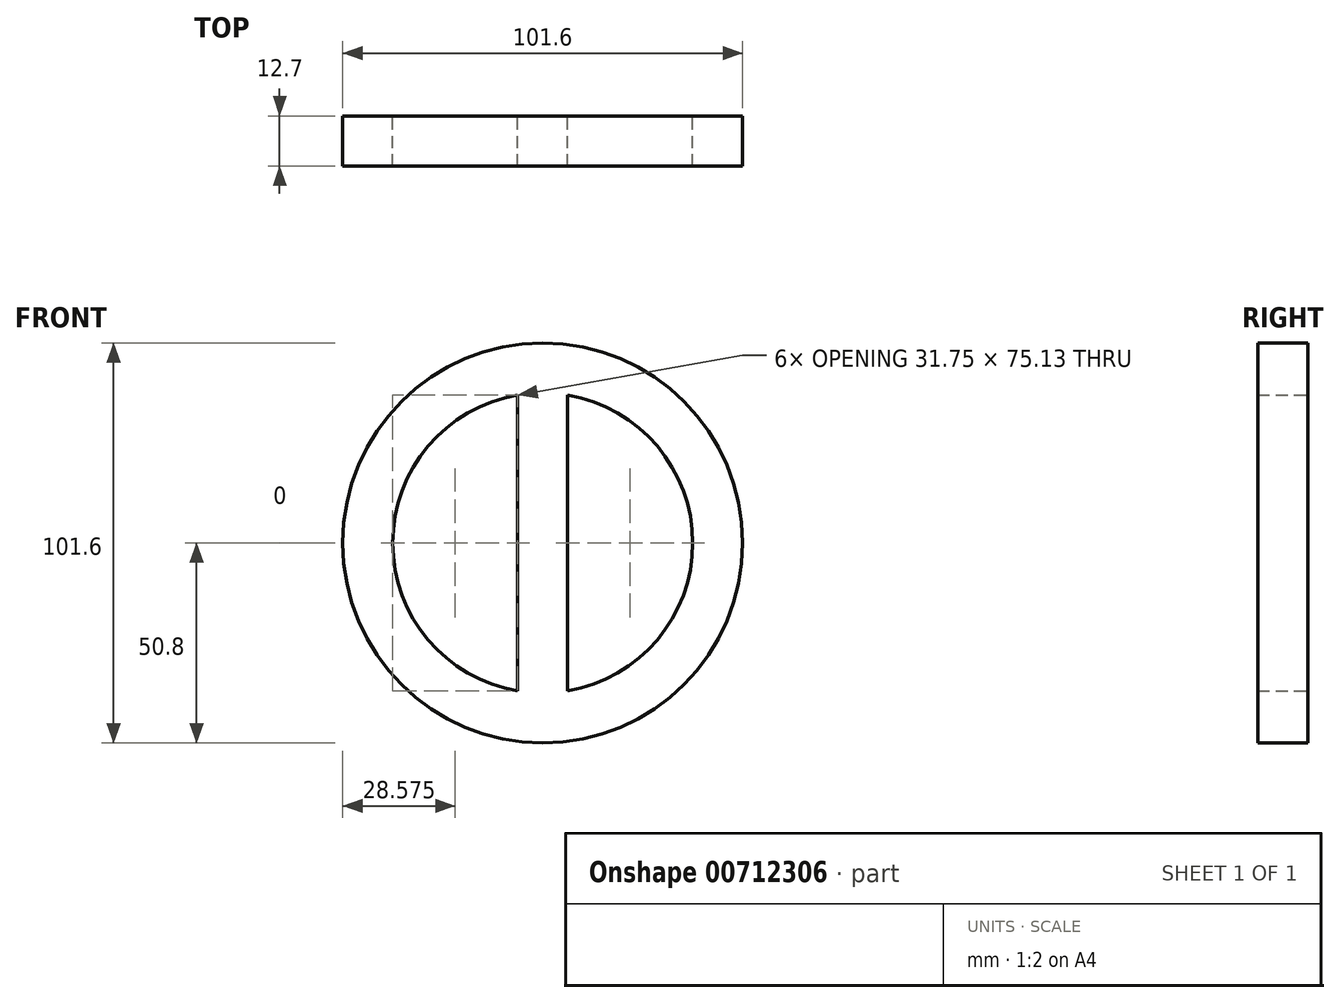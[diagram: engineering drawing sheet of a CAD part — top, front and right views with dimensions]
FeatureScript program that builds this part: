
annotation { "Feature Type Name" : "Feature", "Feature Type Description" : "" }
export const myFeature = defineFeature(function(context is Context, id is Id, definition is map)
    precondition{}
    {
        {
            var Q0;
            Q0=qCreatedBy(makeId("Front.planeOp"),FACE);
            var sketch = newSketch(context, id + "F0", { "sketchPlane" : qUnion([Q0])});
            skArc(sketch, "E0", {"start": v(-6.35, 37.57) * mm, "mid": v(-38.1, 0) * mm, "end": v(-6.35, -37.57) * mm});
            skCircle(sketch, "E1.0", {"center": v(0, 0) * mm, "radius": 50.8 * mm});
            skLineSegment(sketch, "E2.left", {"start": v(-6.35, 37.57) * mm, "end": v(-6.35, -37.57) * mm});
            skLineSegment(sketch, "E2.right", {"start": v(6.35, 37.57) * mm, "end": v(6.35, -37.57) * mm});
            skPoint(sketch, "E2.bottom.end.orphan", {"position": v(6.35, 40.14) * mm});
            skPoint(sketch, "E3.orphan", {"position": v(-6.35, 40.14) * mm});
            skArc(sketch, "E4.trimOffspring", {"start": v(6.35, -37.57) * mm, "mid": v(38.1, 0) * mm, "end": v(6.35, 37.57) * mm});
            skPoint(sketch, "E5.orphan", {"position": v(6.35, -40.14) * mm});
            skPoint(sketch, "E6.orphan", {"position": v(-6.35, -40.14) * mm});
            skSolve(sketch);
        }
        {
            var Q0;
            Q0=makeQuery(id+"F0.imprint","IMPRINT",FACE,{"disambiguationData":[TD([[makeQuery(id+"F0.imprint","IMPRINT",EDGE,{"derivedFrom":sQuery(id+"F0.wireOp",EDGE,"E0")}),-1.0]])]});
            extrude(context, id + "F1", {"entities" : qUnion([Q0]), "depth" : 12.7 * mm, "offsetDistance" : 25.4 * mm});
        }
    });
